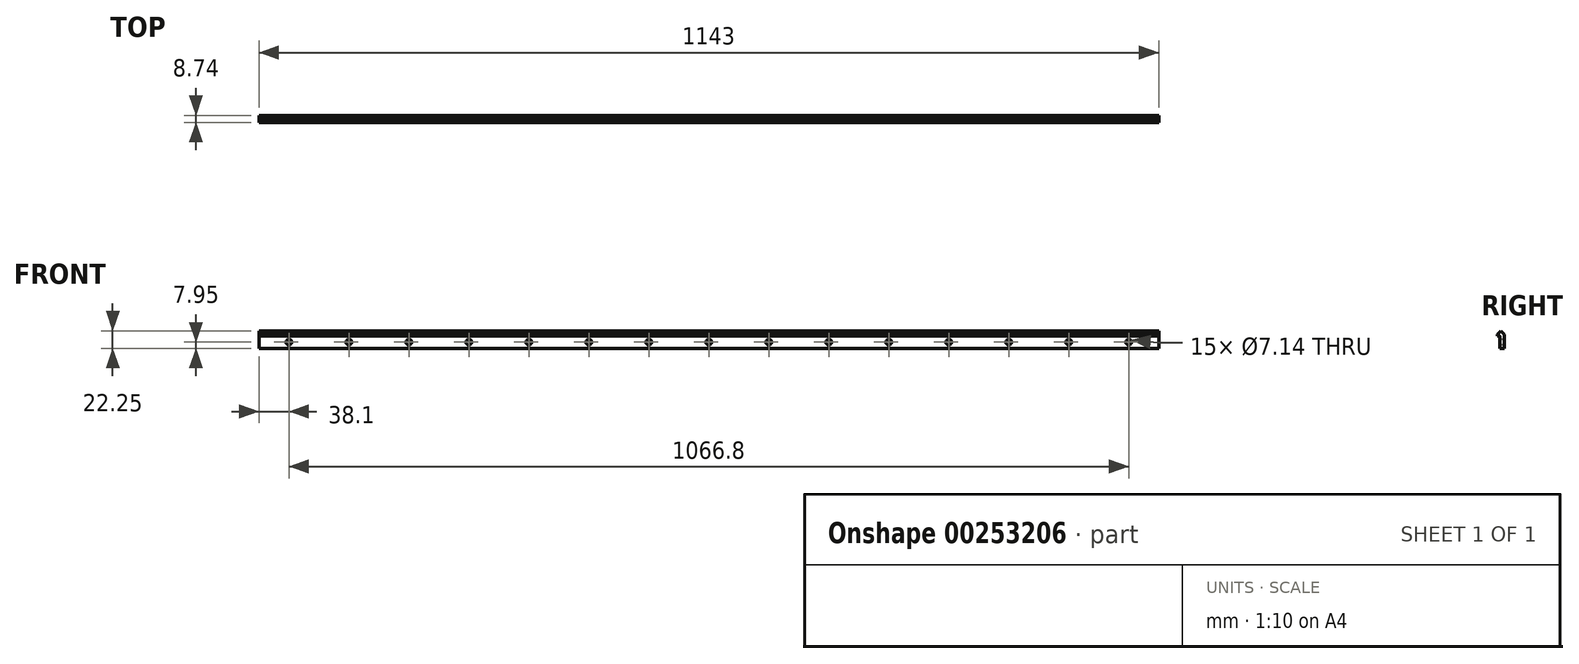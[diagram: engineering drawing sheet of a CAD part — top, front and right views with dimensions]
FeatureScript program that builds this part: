
annotation { "Feature Type Name" : "Feature", "Feature Type Description" : "" }
export const myFeature = defineFeature(function(context is Context, id is Id, definition is map)
    precondition{}
    {
        {
            var Q0;
            Q0=qCreatedBy(makeId("Right.planeOp"),FACE);
            var sketch = newSketch(context, id + "F0", { "sketchPlane" : qUnion([Q0])});
            skLineSegment(sketch, "E0", {"start": v(4.37, -22.25) * mm, "end": v(-1.57, -22.25) * mm});
            skLineSegment(sketch, "E1", {"start": v(-1.57, -22.25) * mm, "end": v(-1.57, -6.54) * mm});
            skLineSegment(sketch, "E2", {"start": v(-1.57, -6.35) * mm, "end": v(-4.37, -6.35) * mm});
            skLineSegment(sketch, "E3", {"start": v(0, 0) * mm, "end": v(4.37, -4.37) * mm});
            skLineSegment(sketch, "E4", {"start": v(0, 0) * mm, "end": v(0, -2.52) * mm, "construction": true});
            skLineSegment(sketch, "E5", {"start": v(4.37, -22.25) * mm, "end": v(4.37, -4.37) * mm});
            skLineSegment(sketch, "E6.MirrorCS", {"start": v(0, 0) * mm, "end": v(-4.37, -4.37) * mm});
            skLineSegment(sketch, "E7", {"start": v(-4.37, -4.37) * mm, "end": v(-4.37, -6.35) * mm});
            skArc(sketch, "E8", {"start": v(-1.57, -6.54) * mm, "mid": v(-1.49, -6.44) * mm, "end": v(-1.58, -6.35) * mm});
            skPoint(sketch, "E8.second.point", {"position": v(-1.57, -6.54) * mm});
            skPoint(sketch, "E8.third.point", {"position": v(-1.49, -6.43) * mm});
            skSolve(sketch);
        }
        {
            var Q0;
            Q0 = qSketchRegion(id + "F0", true);
            extrude(context, id + "F1", {"entities" : qUnion([Q0]), "endBound" : BoundingType.SYMMETRIC, "depth" : 1143 * mm});
        }
        {
            var Q0;
            Q0=makeQuery(id+"F1.opExtrude","SWEPT_FACE",FACE,{"disambiguationData":[OSD([sQuery(id+"F0.wireOp",EDGE,"E1")])]});
            var sketch = newSketch(context, id + "F2", { "sketchPlane" : qUnion([Q0])});
            skLineSegment(sketch, "E9.0", {"start": v(609.6, -14.3) * mm, "end": v(-609.6, -14.3) * mm, "construction": true});
            skCircle(sketch, "E10", {"center": v(0, -14.3) * mm, "radius": 3.57 * mm});
            skCircle(sketch, "E11.1.0.0", {"center": v(76.2, -14.3) * mm, "radius": 3.57 * mm});
            skCircle(sketch, "E11.2.0.0", {"center": v(152.4, -14.3) * mm, "radius": 3.57 * mm});
            skCircle(sketch, "E11.3.0.0", {"center": v(228.6, -14.3) * mm, "radius": 3.57 * mm});
            skCircle(sketch, "E11.4.0.0", {"center": v(304.8, -14.3) * mm, "radius": 3.57 * mm});
            skCircle(sketch, "E11.5.0.0", {"center": v(381, -14.3) * mm, "radius": 3.57 * mm});
            skCircle(sketch, "E11.6.0.0", {"center": v(457.2, -14.3) * mm, "radius": 3.57 * mm});
            skCircle(sketch, "E11.7.0.0", {"center": v(533.4, -14.3) * mm, "radius": 3.57 * mm});
            skLineSegment(sketch, "E11.direction1", {"start": v(0, -14.3) * mm, "end": v(76.2, -14.3) * mm, "construction": true});
            skCircle(sketch, "E12.1.0.0", {"center": v(-76.2, -14.3) * mm, "radius": 3.57 * mm});
            skCircle(sketch, "E12.2.0.0", {"center": v(-152.4, -14.3) * mm, "radius": 3.57 * mm});
            skCircle(sketch, "E12.3.0.0", {"center": v(-228.6, -14.3) * mm, "radius": 3.57 * mm});
            skCircle(sketch, "E12.4.0.0", {"center": v(-304.8, -14.3) * mm, "radius": 3.57 * mm});
            skCircle(sketch, "E12.5.0.0", {"center": v(-381, -14.3) * mm, "radius": 3.57 * mm});
            skCircle(sketch, "E12.6.0.0", {"center": v(-457.2, -14.3) * mm, "radius": 3.57 * mm});
            skCircle(sketch, "E12.7.0.0", {"center": v(-533.4, -14.3) * mm, "radius": 3.57 * mm});
            skLineSegment(sketch, "E12.direction1", {"start": v(0, -14.3) * mm, "end": v(-76.2, -14.3) * mm, "construction": true});
            skSolve(sketch);
        }
        {
            var Q0;
            Q0 = qSketchRegion(id + "F2", true);
            extrude(context, id + "F3", {"entities" : qUnion([Q0]), "operationType" : NewBodyOperationType.REMOVE, "oppositeDirection" : true, "depth" : 25.4 * mm});
        }
    });
